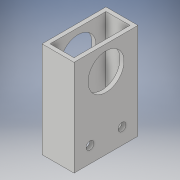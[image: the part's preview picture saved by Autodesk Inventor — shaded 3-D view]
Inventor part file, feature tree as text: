
AUTODESK INVENTOR PART (.ipt)
format: ipt  version: 2018 (Build 220112000, 112)  size: 131,584 bytes
history: native  units: in
note: dims shown in document units (in); Inventor stores cm internally (conversion verified against a paired STEP export)
features: extrude x2, sketch x2
ambient origin geometry x8: Origin, YZ Plane, XZ Plane, XY Plane, X Axis, Y Axis, Z Axis, Center Point
bodies: Solid1 (feature_tree)
feature tree (4):
  extrude  "Extrusion1"  Depth=1.0in
  extrude  "Extrusion2"  Depth=0.125in
  sketch  "Sketch1"  dims[d0=2.0in d1=1.0in]
  sketch  "Sketch2"  dims[d2=0.125in d3=0.125in d4=0.125in d5=0.125in d6=3.0in d7=0.0in d8=0.5in d9=0.25in d10=0.5in d11=0.5in d12=0.5in d13=0.25in d14=1.125in d15=0.75in d16=1.0in d17=3.0in d18=0.0in]
